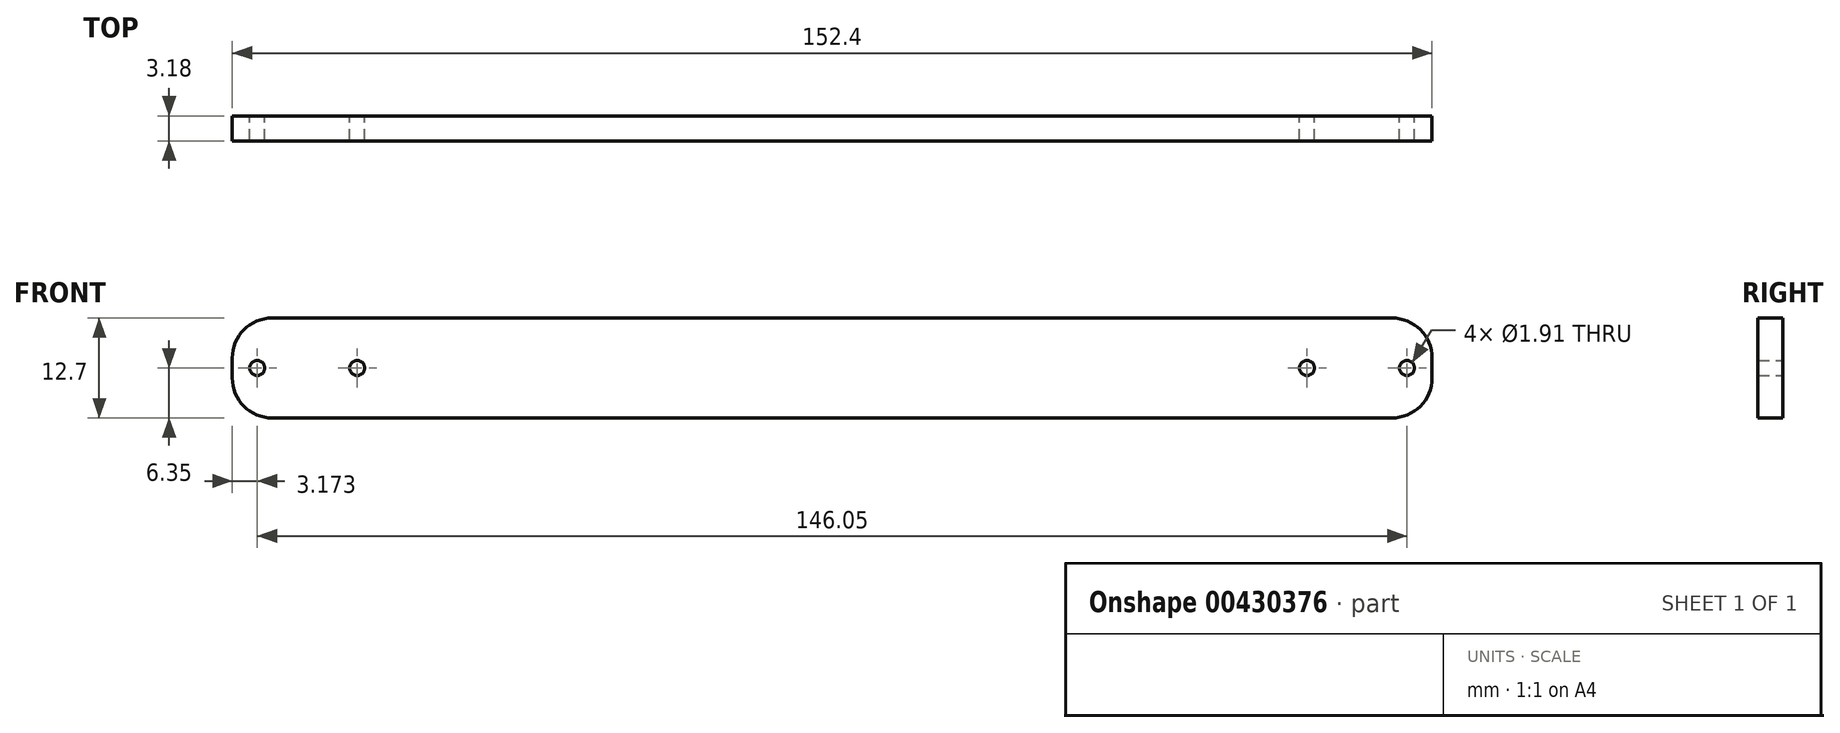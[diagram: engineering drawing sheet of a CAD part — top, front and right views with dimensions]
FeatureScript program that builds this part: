
annotation { "Feature Type Name" : "Feature", "Feature Type Description" : "" }
export const myFeature = defineFeature(function(context is Context, id is Id, definition is map)
    precondition{}
    {
        {
            var Q0;
            Q0=qCreatedBy(makeId("Front.planeOp"),FACE);
            var sketch = newSketch(context, id + "F0", { "sketchPlane" : qUnion([Q0])});
            skLineSegment(sketch, "E0.bottom", {"start": v(101.18, 0) * mm, "end": v(-51.22, 0) * mm});
            skLineSegment(sketch, "E0.top", {"start": v(101.18, 12.7) * mm, "end": v(-51.22, 12.7) * mm});
            skLineSegment(sketch, "E0.left", {"start": v(101.18, 0) * mm, "end": v(101.18, 12.7) * mm});
            skLineSegment(sketch, "E0.right", {"start": v(-51.22, 0) * mm, "end": v(-51.22, 12.7) * mm});
            skCircle(sketch, "E1", {"center": v(98, 6.35) * mm, "radius": 0.95 * mm});
            skCircle(sketch, "E2", {"center": v(85.3, 6.35) * mm, "radius": 0.95 * mm});
            skCircle(sketch, "E3", {"center": v(-48.05, 6.35) * mm, "radius": 0.95 * mm});
            skCircle(sketch, "E4", {"center": v(-35.35, 6.35) * mm, "radius": 0.95 * mm});
            skSolve(sketch);
        }
        {
            var Q0;
            Q0=makeQuery(id+"F0.imprint","IMPRINT",FACE,{"disambiguationData":[TD([[makeQuery(id+"F0.imprint","IMPRINT",EDGE,{"derivedFrom":sQuery(id+"F0.wireOp",EDGE,"E0.bottom")}),-1.0]])]});
            extrude(context, id + "F1", {"entities" : qUnion([Q0]), "depth" : 3.17 * mm});
        }
        {
            var Q0;
            Q0=makeQuery(id+"F1.opExtrude","SWEPT_EDGE",EDGE,{"disambiguationData":[OSD([sQuery(id+"F0.wireOp",EDGE,"E0.top"),sQuery(id+"F0.wireOp",EDGE,"E0.left")])]});
            var Q1;
            Q1=makeQuery(id+"F1.opExtrude","SWEPT_EDGE",EDGE,{"disambiguationData":[OSD([sQuery(id+"F0.wireOp",EDGE,"E0.bottom"),sQuery(id+"F0.wireOp",EDGE,"E0.left")])]});
            var Q2;
            Q2=makeQuery(id+"F1.opExtrude","SWEPT_EDGE",EDGE,{"disambiguationData":[OSD([sQuery(id+"F0.wireOp",EDGE,"E0.top"),sQuery(id+"F0.wireOp",EDGE,"E0.right")])]});
            var Q3;
            Q3=makeQuery(id+"F1.opExtrude","SWEPT_EDGE",EDGE,{"disambiguationData":[OSD([sQuery(id+"F0.wireOp",EDGE,"E0.bottom"),sQuery(id+"F0.wireOp",EDGE,"E0.right")])]});
            fillet(context, id + "F2", {"entities" : qUnion([Q0, Q1, Q2, Q3]), "radius" : 5.08 * mm, "tangentPropagation" : true, "allowEdgeOverflow" : false});
        }
    });
